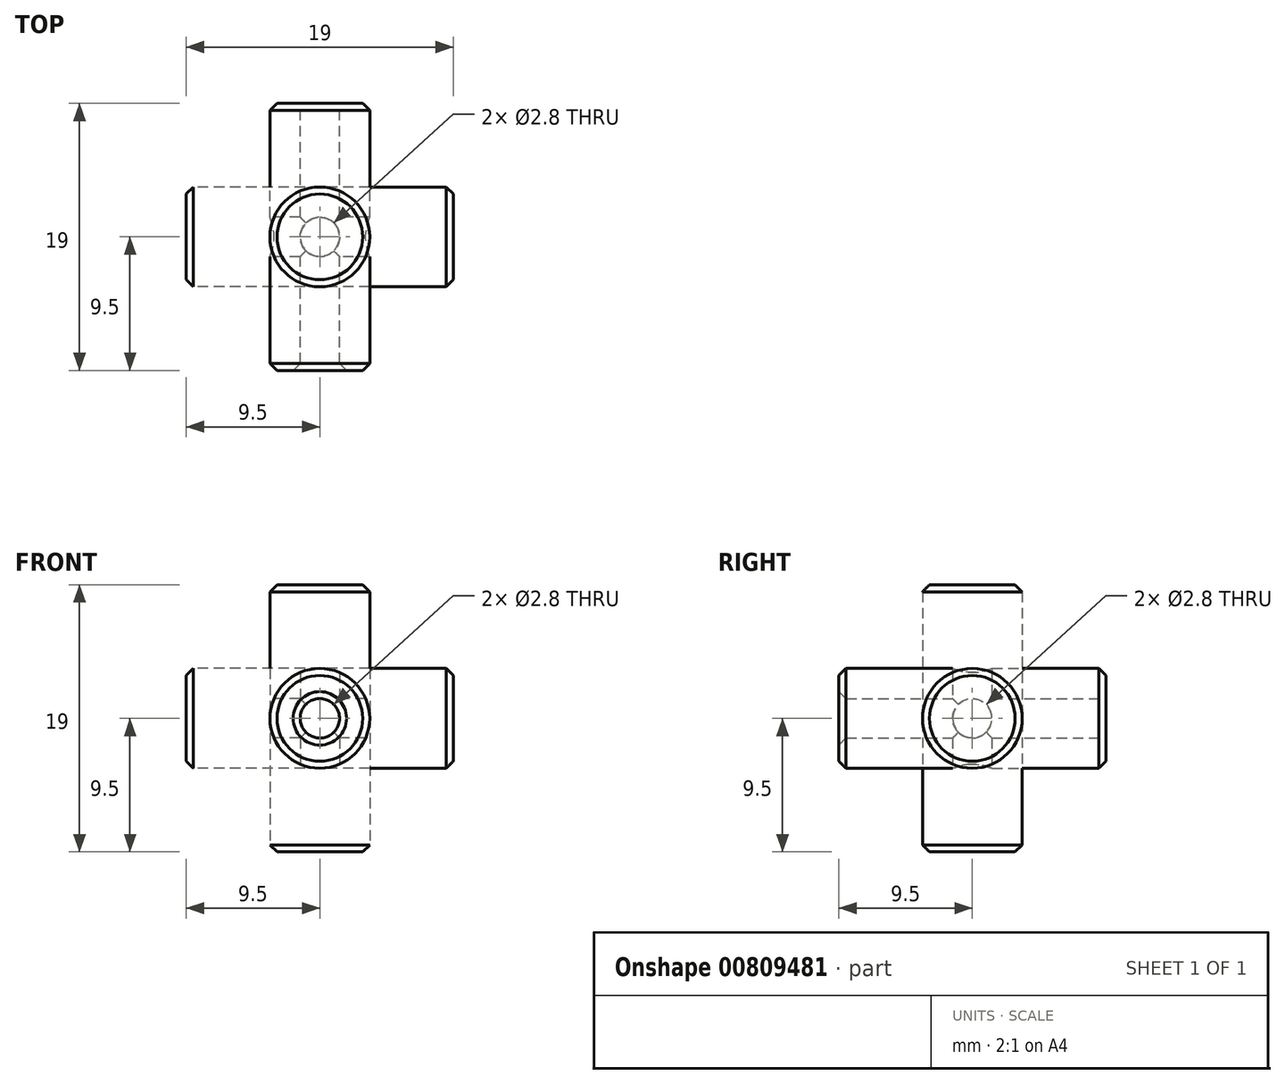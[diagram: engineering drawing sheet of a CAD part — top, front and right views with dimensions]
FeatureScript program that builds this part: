
annotation { "Feature Type Name" : "Feature", "Feature Type Description" : "" }
export const myFeature = defineFeature(function(context is Context, id is Id, definition is map)
    precondition{}
    {
        {
            var Q0;
            Q0=qCreatedBy(makeId("Front.planeOp"),FACE);
            var sketch = newSketch(context, id + "F0", { "sketchPlane" : qUnion([Q0])});
            skCircle(sketch, "E0", {"center": v(0, 0) * mm, "radius": 3.55 * mm});
            skSolve(sketch);
        }
        {
            var Q0;
            Q0 = qSketchRegion(id + "F0", true);
            extrude(context, id + "F1", {"entities" : qUnion([Q0]), "endBound" : BoundingType.SYMMETRIC, "depth" : 19 * mm, "offsetDistance" : 25 * mm});
        }
        {
            var Q0;
            Q0=qCreatedBy(makeId("Front.planeOp"),FACE);
            var sketch = newSketch(context, id + "F2", { "sketchPlane" : qUnion([Q0])});
            skCircle(sketch, "E1", {"center": v(0, 0) * mm, "radius": 1.4 * mm});
            skSolve(sketch);
        }
        {
            var Q0;
            Q0 = qSketchRegion(id + "F2", true);
            extrude(context, id + "F3", {"entities" : qUnion([Q0]), "endBound" : BoundingType.SYMMETRIC, "depth" : 20 * mm, "offsetDistance" : 25 * mm});
        }
        {
            var Q0;
            Q0=qCreatedBy(makeId("Front.planeOp"),FACE);
            var sketch = newSketch(context, id + "F4", { "sketchPlane" : qUnion([Q0])});
            skLineSegment(sketch, "E2.bottom", {"start": v(0, 0) * mm, "end": v(10, 0) * mm});
            skLineSegment(sketch, "E2.top", {"start": v(0, 10) * mm, "end": v(10, 10) * mm});
            skLineSegment(sketch, "E2.left", {"start": v(0, 0) * mm, "end": v(0, 10) * mm});
            skLineSegment(sketch, "E2.right", {"start": v(10, 0) * mm, "end": v(10, 10) * mm});
            skSolve(sketch);
        }
        {
            var Q0;
            Q0=makeQuery(id+"F4.imprint","IMPRINT",FACE,{"disambiguationData":[TD([[makeQuery(id+"F4.imprint","IMPRINT",EDGE,{"derivedFrom":sQuery(id+"F4.wireOp",EDGE,"E2.bottom")}),1.0]])]});
            extrude(context, id + "F5", {"entities" : qUnion([Q0]), "depth" : 10 * mm, "offsetDistance" : 25 * mm});
        }
        {
            var Q0;
            Q0=qCreatedBy(makeId("Origin.pointOp"),VERTEX);
            var Q1;
            Q1=makeQuery(id+"F5.opExtrude","CAP_VERTEX",VERTEX,{"disambiguationData":[OSD([sQuery(id+"F4.wireOp",EDGE,"E2.top"),sQuery(id+"F4.wireOp",EDGE,"E2.right")])],"isStart":false});
            var Q2;
            Q2=makeQuery(id+"F5.opExtrude","CAP_VERTEX",VERTEX,{"disambiguationData":[OSD([sQuery(id+"F4.wireOp",EDGE,"E2.bottom"),sQuery(id+"F4.wireOp",EDGE,"E2.right")])],"isStart":false});
            cPlane(context, id + "F6", {"entities" : qUnion([Q0, Q1, Q2]), "cplaneType" : CPlaneType.THREE_POINT, "offset" : 25 * mm, "width" : 150 * mm, "height" : 150 * mm});
        }
        {
            var Q0;
            Q0=qCreatedBy(id+"F6.planeOp",FACE);
            var sketch = newSketch(context, id + "F7", { "sketchPlane" : qUnion([Q0])});
            skLineSegment(sketch, "E3", {"start": v(0, 0) * mm, "end": v(14.14, 10) * mm});
            skSolve(sketch);
        }
        {
            var Q0;
            Q0=makeQuery(id+"F5.opExtrude","SWEPT_BODY",BODY,{"disambiguationData":[OSD([sQuery(id+"F4.wireOp",EDGE,"E2.bottom"),sQuery(id+"F4.wireOp",EDGE,"E2.top"),sQuery(id+"F4.wireOp",EDGE,"E2.left"),sQuery(id+"F4.wireOp",EDGE,"E2.right")])]});
            deleteBodies(context, id + "F8", {"entities" : qUnion([Q0])});
        }
        {
            var Q0;
            Q0=makeQuery(id+"F3.opExtrude","SWEPT_BODY",BODY,{"disambiguationData":[OSD([sQuery(id+"F2.wireOp",EDGE,"E1")])]});
            var Q1;
            Q1=makeQuery(id+"F1.opExtrude","SWEPT_BODY",BODY,{"disambiguationData":[OSD([sQuery(id+"F0.wireOp",EDGE,"E0")])]});
            var Q2;
            Q2=sQuery(id+"F7.wireOp",EDGE,"E3");
            circularPattern(context, id + "F9", {"entities" : qUnion([Q0, Q1]), "axis" : qUnion([Q2]), "angle" : 360 * degree, "instanceCount" : 3, "equalSpace" : true});
        }
        {
            var Q0;
            Q0=makeQuery(id+"F3.opExtrude","SWEPT_BODY",BODY,{"disambiguationData":[OSD([sQuery(id+"F2.wireOp",EDGE,"E1")])]});
            var Q1;
            Q1=makeQuery(id+"F9.opPattern","COPY",BODY,{"derivedFrom":makeQuery(id+"F3.opExtrude","SWEPT_BODY",BODY,{"disambiguationData":[OSD([sQuery(id+"F2.wireOp",EDGE,"E1")])]}),"instanceName":"2"});
            var Q2;
            Q2=makeQuery(id+"F9.opPattern","COPY",BODY,{"derivedFrom":makeQuery(id+"F3.opExtrude","SWEPT_BODY",BODY,{"disambiguationData":[OSD([sQuery(id+"F2.wireOp",EDGE,"E1")])]}),"instanceName":"1"});
            var Q3;
            Q3=makeQuery(id+"F1.opExtrude","SWEPT_BODY",BODY,{"disambiguationData":[OSD([sQuery(id+"F0.wireOp",EDGE,"E0")])]});
            booleanBodies(context, id + "F10", {"operationType" : BooleanOperationType.SUBTRACTION, "tools" : qUnion([Q0, Q1, Q2]), "targets" : qUnion([Q3])});
        }
        {
            var Q0;
            Q0=makeQuery(id+"F1.opExtrude","CAP_FACE",FACE,{"disambiguationData":[OSD([sQuery(id+"F0.wireOp",EDGE,"E0")])],"isStart":false});
            var Q1;
            Q1=makeQuery(id+"F1.opExtrude","CAP_EDGE",EDGE,{"disambiguationData":[OSD([sQuery(id+"F0.wireOp",EDGE,"E0")])],"isStart":true});
            var Q2;
            Q2=makeQuery(id+"F9.opPattern","COPY",EDGE,{"derivedFrom":makeQuery(id+"F1.opExtrude","CAP_EDGE",EDGE,{"disambiguationData":[OSD([sQuery(id+"F0.wireOp",EDGE,"E0")])],"isStart":true}),"instanceName":"2"});
            var Q3;
            Q3=makeQuery(id+"F9.opPattern","COPY",EDGE,{"derivedFrom":makeQuery(id+"F1.opExtrude","CAP_EDGE",EDGE,{"disambiguationData":[OSD([sQuery(id+"F0.wireOp",EDGE,"E0")])],"isStart":false}),"instanceName":"1"});
            var Q4;
            Q4=makeQuery(id+"F9.opPattern","COPY",EDGE,{"derivedFrom":makeQuery(id+"F1.opExtrude","CAP_EDGE",EDGE,{"disambiguationData":[OSD([sQuery(id+"F0.wireOp",EDGE,"E0")])],"isStart":true}),"instanceName":"1"});
            var Q5;
            Q5=makeQuery(id+"F9.opPattern","COPY",EDGE,{"derivedFrom":makeQuery(id+"F1.opExtrude","CAP_EDGE",EDGE,{"disambiguationData":[OSD([sQuery(id+"F0.wireOp",EDGE,"E0")])],"isStart":false}),"instanceName":"2"});
            chamfer(context, id + "F11", {"entities" : qUnion([Q0, Q1, Q2, Q3, Q4, Q5]), "width" : 0.5 * mm, "tangentPropagation" : true});
        }
    });
